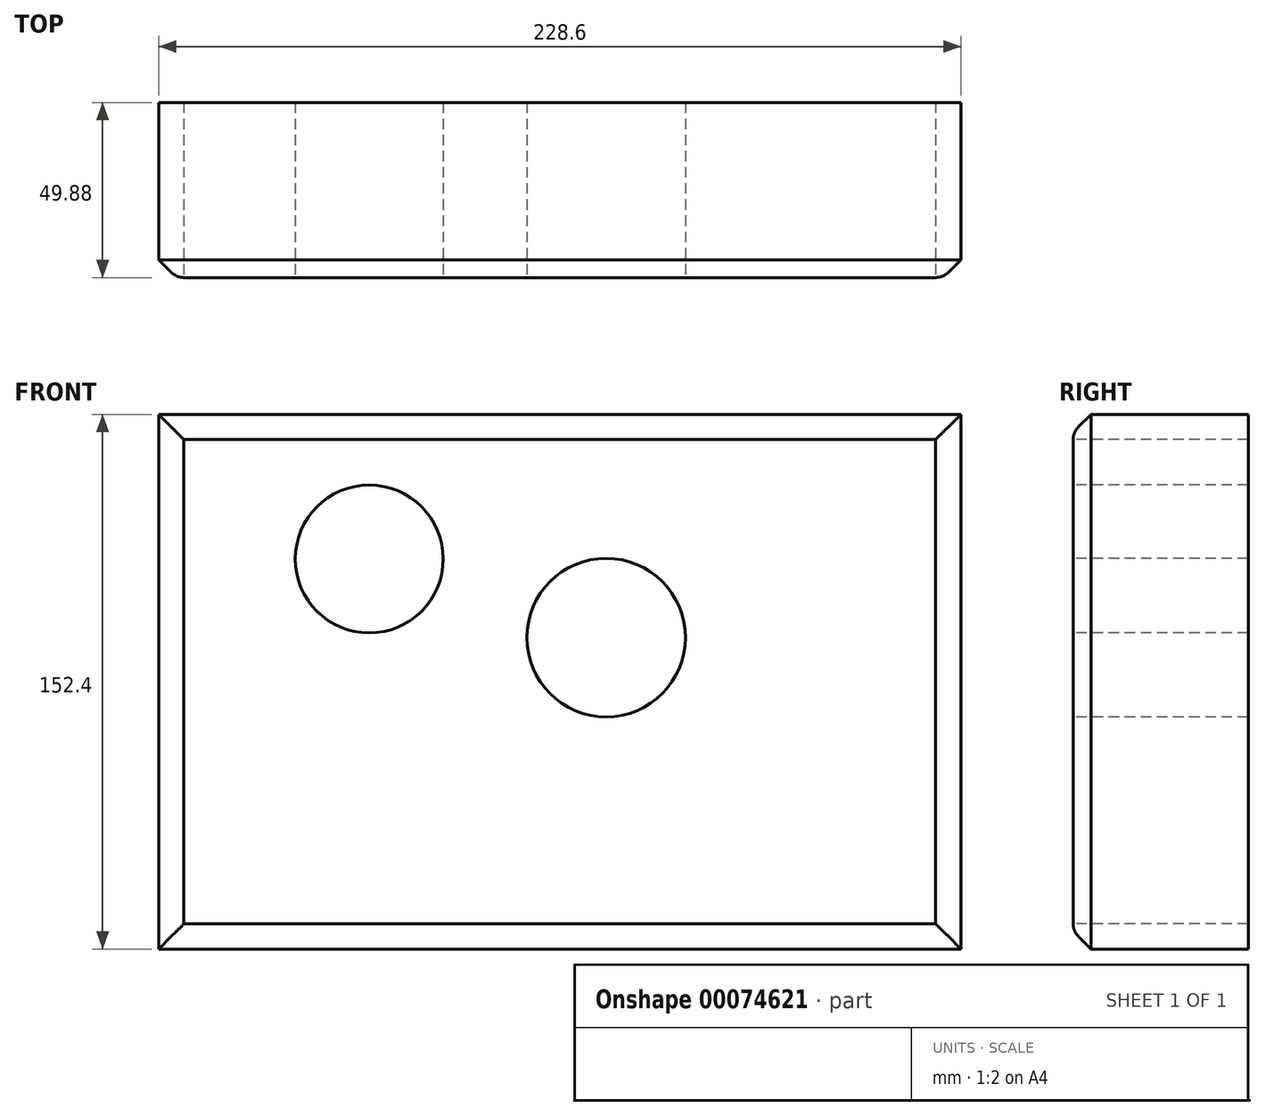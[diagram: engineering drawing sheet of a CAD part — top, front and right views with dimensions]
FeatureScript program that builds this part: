
annotation { "Feature Type Name" : "Feature", "Feature Type Description" : "" }
export const myFeature = defineFeature(function(context is Context, id is Id, definition is map)
    precondition{}
    {
        {
            var Q0;
            Q0=qCreatedBy(makeId("Front.planeOp"),FACE);
            var sketch = newSketch(context, id + "F0", { "sketchPlane" : qUnion([Q0])});
            skLineSegment(sketch, "E0.bottom", {"start": v(-127.5, 55.27) * mm, "end": v(101.1, 55.27) * mm});
            skLineSegment(sketch, "E0.top", {"start": v(-127.5, -97.13) * mm, "end": v(101.1, -97.13) * mm});
            skLineSegment(sketch, "E0.left", {"start": v(-127.5, 55.27) * mm, "end": v(-127.5, -97.13) * mm});
            skLineSegment(sketch, "E0.right", {"start": v(101.1, 55.27) * mm, "end": v(101.1, -97.13) * mm});
            skSolve(sketch);
        }
        {
            var Q0;
            Q0=makeQuery(id+"F0.imprint","IMPRINT",FACE,{"disambiguationData":[TD([[makeQuery(id+"F0.imprint","IMPRINT",EDGE,{"derivedFrom":sQuery(id+"F0.wireOp",EDGE,"E0.bottom")}),-1.0]])]});
            extrude(context, id + "F1", {"entities" : qUnion([Q0]), "depth" : 49.88 * mm});
        }
        {
            var Q0;
            Q0=makeQuery(id+"F1.opExtrude","CAP_EDGE",EDGE,{"disambiguationData":[OSD([sQuery(id+"F0.wireOp",EDGE,"E0.bottom")])],"isStart":false});
            var Q1;
            Q1=makeQuery(id+"F1.opExtrude","CAP_EDGE",EDGE,{"disambiguationData":[OSD([sQuery(id+"F0.wireOp",EDGE,"E0.right")])],"isStart":false});
            var Q2;
            Q2=makeQuery(id+"F1.opExtrude","CAP_EDGE",EDGE,{"disambiguationData":[OSD([sQuery(id+"F0.wireOp",EDGE,"E0.top")])],"isStart":false});
            var Q3;
            Q3=makeQuery(id+"F1.opExtrude","CAP_EDGE",EDGE,{"disambiguationData":[OSD([sQuery(id+"F0.wireOp",EDGE,"E0.left")])],"isStart":false});
            chamfer(context, id + "F2", {"entities" : qUnion([Q0, Q1, Q2, Q3]), "width" : 5.08 * mm, "tangentPropagation" : true});
        }
        {
            var Q0;
            {var subQ0=sQuery(id+"F0.wireOp",EDGE,"E0.bottom");Q0=makeQuery(id+"F2.opChamfer","BLEND_EDGE",EDGE,{"blendedFrom":[makeQuery(id+"F1.opExtrude","CAP_EDGE",EDGE,{"disambiguationData":[OSD([subQ0])],"isStart":false}),makeQuery(id+"F1.opExtrude","CAP_FACE",FACE,{"disambiguationData":[OSD([subQ0,sQuery(id+"F0.wireOp",EDGE,"E0.top"),sQuery(id+"F0.wireOp",EDGE,"E0.left"),sQuery(id+"F0.wireOp",EDGE,"E0.right")])],"isStart":false})],"blendedInto":[makeQuery(id+"F1.opExtrude","CAP_FACE",FACE,{"disambiguationData":[OSD([subQ0,sQuery(id+"F0.wireOp",EDGE,"E0.top"),sQuery(id+"F0.wireOp",EDGE,"E0.left"),sQuery(id+"F0.wireOp",EDGE,"E0.right")])],"isStart":false})]});}
            var Q1;
            {var subQ0=sQuery(id+"F0.wireOp",EDGE,"E0.left");Q1=makeQuery(id+"F2.opChamfer","BLEND_EDGE",EDGE,{"blendedFrom":[makeQuery(id+"F1.opExtrude","CAP_EDGE",EDGE,{"disambiguationData":[OSD([subQ0])],"isStart":false}),makeQuery(id+"F1.opExtrude","CAP_FACE",FACE,{"disambiguationData":[OSD([sQuery(id+"F0.wireOp",EDGE,"E0.bottom"),sQuery(id+"F0.wireOp",EDGE,"E0.top"),subQ0,sQuery(id+"F0.wireOp",EDGE,"E0.right")])],"isStart":false})],"blendedInto":[makeQuery(id+"F1.opExtrude","CAP_FACE",FACE,{"disambiguationData":[OSD([sQuery(id+"F0.wireOp",EDGE,"E0.bottom"),sQuery(id+"F0.wireOp",EDGE,"E0.top"),subQ0,sQuery(id+"F0.wireOp",EDGE,"E0.right")])],"isStart":false})]});}
            var Q2;
            {var subQ0=sQuery(id+"F0.wireOp",EDGE,"E0.right");Q2=makeQuery(id+"F2.opChamfer","BLEND_EDGE",EDGE,{"blendedFrom":[makeQuery(id+"F1.opExtrude","CAP_EDGE",EDGE,{"disambiguationData":[OSD([subQ0])],"isStart":false}),makeQuery(id+"F1.opExtrude","CAP_FACE",FACE,{"disambiguationData":[OSD([sQuery(id+"F0.wireOp",EDGE,"E0.bottom"),sQuery(id+"F0.wireOp",EDGE,"E0.top"),sQuery(id+"F0.wireOp",EDGE,"E0.left"),subQ0])],"isStart":false})],"blendedInto":[makeQuery(id+"F1.opExtrude","CAP_FACE",FACE,{"disambiguationData":[OSD([sQuery(id+"F0.wireOp",EDGE,"E0.bottom"),sQuery(id+"F0.wireOp",EDGE,"E0.top"),sQuery(id+"F0.wireOp",EDGE,"E0.left"),subQ0])],"isStart":false})]});}
            var Q3;
            {var subQ0=sQuery(id+"F0.wireOp",EDGE,"E0.top");Q3=makeQuery(id+"F2.opChamfer","BLEND_EDGE",EDGE,{"blendedFrom":[makeQuery(id+"F1.opExtrude","CAP_EDGE",EDGE,{"disambiguationData":[OSD([subQ0])],"isStart":false}),makeQuery(id+"F1.opExtrude","CAP_FACE",FACE,{"disambiguationData":[OSD([sQuery(id+"F0.wireOp",EDGE,"E0.bottom"),subQ0,sQuery(id+"F0.wireOp",EDGE,"E0.left"),sQuery(id+"F0.wireOp",EDGE,"E0.right")])],"isStart":false})],"blendedInto":[makeQuery(id+"F1.opExtrude","CAP_FACE",FACE,{"disambiguationData":[OSD([sQuery(id+"F0.wireOp",EDGE,"E0.bottom"),subQ0,sQuery(id+"F0.wireOp",EDGE,"E0.left"),sQuery(id+"F0.wireOp",EDGE,"E0.right")])],"isStart":false})]});}
            fillet(context, id + "F3", {"entities" : qUnion([Q0, Q1, Q2, Q3]), "radius" : 5.08 * mm, "tangentPropagation" : true, "allowEdgeOverflow" : false});
        }
        {
            var Q0;
            Q0=makeQuery(id+"F1.opExtrude","CAP_FACE",FACE,{"disambiguationData":[OSD([sQuery(id+"F0.wireOp",EDGE,"E0.bottom"),sQuery(id+"F0.wireOp",EDGE,"E0.top"),sQuery(id+"F0.wireOp",EDGE,"E0.left"),sQuery(id+"F0.wireOp",EDGE,"E0.right")])],"isStart":false});
            var sketch = newSketch(context, id + "F4", { "sketchPlane" : qUnion([Q0])});
            skCircle(sketch, "E1", {"center": v(-67.5, 14.04) * mm, "radius": 21.08 * mm});
            skSolve(sketch);
        }
        {
            var Q0;
            Q0=makeQuery(id+"F4.imprint","IMPRINT",FACE,{"disambiguationData":[TD([[makeQuery(id+"F4.imprint","IMPRINT",EDGE,{"derivedFrom":sQuery(id+"F4.wireOp",EDGE,"E1")}),-1.0]])]});
            var sketch = newSketch(context, id + "F5", { "sketchPlane" : qUnion([Q0])});
            skCircle(sketch, "E2", {"center": v(0, -8.36) * mm, "radius": 22.6 * mm});
            skSolve(sketch);
        }
        {
            var Q0;
            Q0=makeQuery(id+"F5.imprint","IMPRINT",FACE,{"disambiguationData":[TD([[makeQuery(id+"F5.imprint","IMPRINT",EDGE,{"derivedFrom":sQuery(id+"F5.wireOp",EDGE,"E2")}),-1.0]])]});
            extrude(context, id + "F6", {"entities" : qUnion([Q0]), "operationType" : NewBodyOperationType.REMOVE, "oppositeDirection" : true, "depth" : 221.82 * mm});
        }
    });
